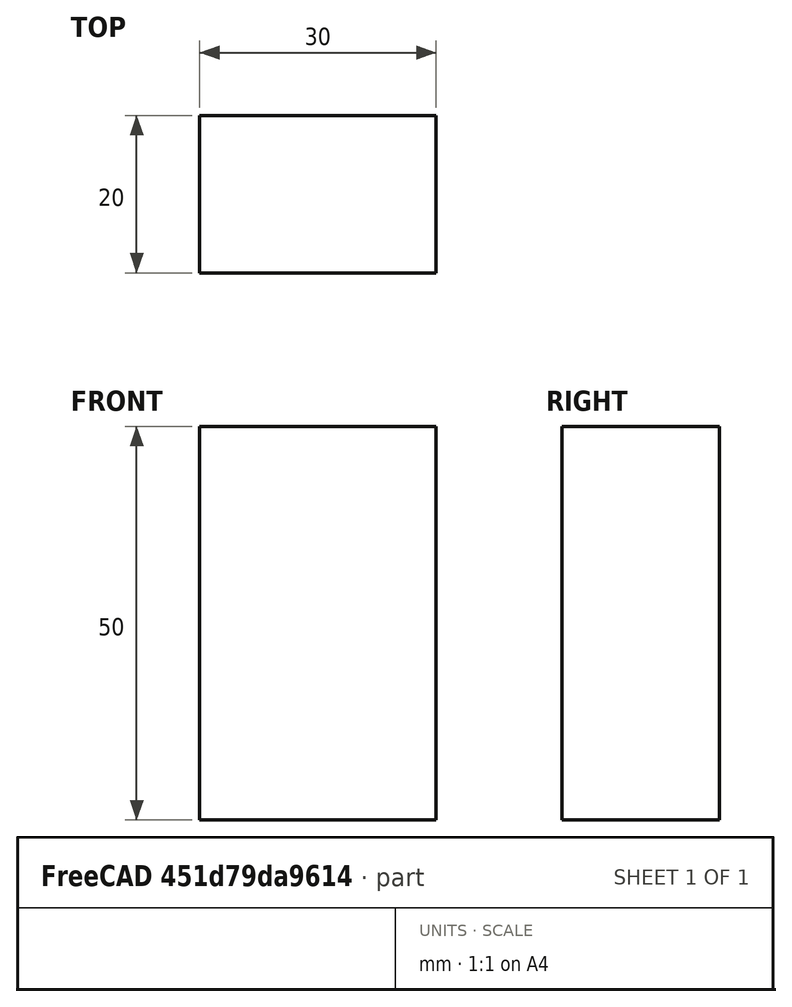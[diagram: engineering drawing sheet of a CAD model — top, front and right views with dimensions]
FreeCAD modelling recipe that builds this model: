
FCSTD DOCUMENT  (FreeCAD 0.14R3700 (Git))
Label: BR_9V
License: CC-BY 3.0
LicenseURL: http://creativecommons.org/licenses/by/3.0/
objects: Sketcher::SketchObject×1, Part::Extrusion×1, Part::Feature×1
note: 3 computed .brp shape members not serialized (recipe doc carries the construction recipe); baked Part::Feature solids carry a one-line shape summary decoded from their .brp

FEATURE [Sketcher::SketchObject] Sketch
  sketch-geometry (4):
    g0: LineSegment StartX=-15 StartY=10 StartZ=0 EndX=15 EndY=10 EndZ=0
    g1: LineSegment StartX=15 StartY=10 StartZ=0 EndX=15 EndY=-10 EndZ=0
    g2: LineSegment StartX=15 StartY=-10 StartZ=0 EndX=-15 EndY=-10 EndZ=0
    g3: LineSegment StartX=-15 StartY=-10 StartZ=0 EndX=-15 EndY=10 EndZ=0
  constraints (12):
    c: Coincident(g0,g1)
    c: Coincident(g1,g2)
    c: Coincident(g2,g3)
    c: Coincident(g3,g0)
    c: Horizontal(g0)
    c: Horizontal(g2)
    c: Vertical(g1)
    c: Vertical(g3)
    c: Symmetric(g0,g2,g-1)
    c: Symmetric(g0,g0,g-2)
    c: DistanceX(g0) = 30
    c: DistanceY(g3) = 20
FEATURE [Part::Extrusion] Extrude
  Base = -> Sketch
  Dir = (0,0,50)
  Solid = true
FEATURE [Part::Feature] Extrude001  label="Pile9V"
  shape: bbox 30 x 20 x 50 mm, 6 faces (baked)
